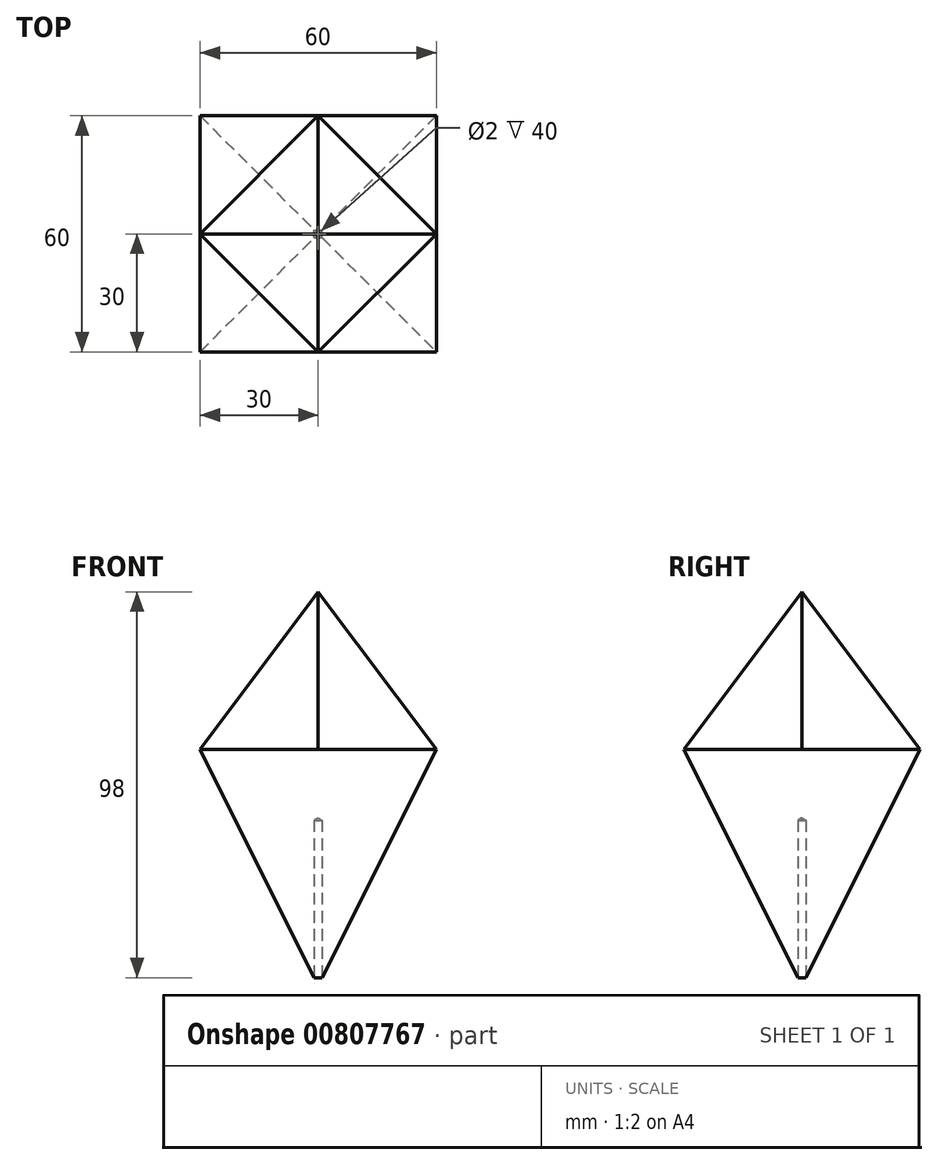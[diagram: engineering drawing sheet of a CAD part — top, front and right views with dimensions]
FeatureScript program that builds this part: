
annotation { "Feature Type Name" : "Feature", "Feature Type Description" : "" }
export const myFeature = defineFeature(function(context is Context, id is Id, definition is map)
    precondition{}
    {
        {
            var Q0;
            Q0=qCreatedBy(makeId("Top.planeOp"),FACE);
            cPlane(context, id + "F0", {"entities" : qUnion([Q0]), "cplaneType" : CPlaneType.OFFSET, "offset" : 60 * mm, "width" : 152.4 * mm, "height" : 152.4 * mm});
        }
        {
            var Q0;
            Q0=qCreatedBy(id+"F0.planeOp",FACE);
            var sketch = newSketch(context, id + "F1", { "sketchPlane" : qUnion([Q0])});
            skLineSegment(sketch, "E0.bottom", {"start": v(-30, 30) * mm, "end": v(30, 30) * mm});
            skLineSegment(sketch, "E0.top", {"start": v(-30, -30) * mm, "end": v(30, -30) * mm});
            skLineSegment(sketch, "E0.left", {"start": v(-30, 30) * mm, "end": v(-30, -30) * mm});
            skLineSegment(sketch, "E0.right", {"start": v(30, 30) * mm, "end": v(30, -30) * mm});
            skPoint(sketch, "E0.middle", {"position": v(0, 0) * mm});
            skLineSegment(sketch, "E1", {"start": v(-30, 0) * mm, "end": v(0, 30) * mm});
            skLineSegment(sketch, "E2", {"start": v(0, 30) * mm, "end": v(30, 0) * mm});
            skLineSegment(sketch, "E3", {"start": v(30, 0) * mm, "end": v(0, -30) * mm});
            skLineSegment(sketch, "E4", {"start": v(0, -30) * mm, "end": v(-30, 0) * mm});
            skSolve(sketch);
        }
        {
            var Q0;
            Q0=qCreatedBy(makeId("Top.planeOp"),FACE);
            cPlane(context, id + "F2", {"entities" : qUnion([Q0]), "cplaneType" : CPlaneType.OFFSET, "offset" : 100 * mm, "width" : 150 * mm, "height" : 150 * mm});
        }
        {
            var Q0;
            Q0=qCreatedBy(id+"F2.planeOp",FACE);
            var sketch = newSketch(context, id + "F3", { "sketchPlane" : qUnion([Q0])});
            skPoint(sketch, "E5.0", {"position": v(0, 0) * mm});
            skSolve(sketch);
        }
        {
            var Q0;
            Q0=qCreatedBy(makeId("Top.planeOp"),FACE);
            var sketch = newSketch(context, id + "F4", { "sketchPlane" : qUnion([Q0])});
            skPoint(sketch, "E6.0", {"position": v(0, 0) * mm});
            skLineSegment(sketch, "E7", {"start": v(0, 0) * mm, "end": v(-2.79, 22.45) * mm});
            skSolve(sketch);
        }
        {
            var Q0;
            Q0=qCreatedBy(makeId("Top.planeOp"),FACE);
            cPlane(context, id + "F5", {"entities" : qUnion([Q0]), "cplaneType" : CPlaneType.OFFSET, "offset" : 2 * mm, "width" : 150 * mm, "height" : 150 * mm});
        }
        {
            var Q0;
            Q0=qCreatedBy(id+"F5.planeOp",FACE);
            var sketch = newSketch(context, id + "F6", { "sketchPlane" : qUnion([Q0])});
            skLineSegment(sketch, "E8.bottom", {"start": v(-1, -1) * mm, "end": v(1, -1) * mm});
            skLineSegment(sketch, "E8.top", {"start": v(-1, 1) * mm, "end": v(1, 1) * mm});
            skLineSegment(sketch, "E8.left", {"start": v(-1, -1) * mm, "end": v(-1, 1) * mm});
            skLineSegment(sketch, "E8.right", {"start": v(1, -1) * mm, "end": v(1, 1) * mm});
            skPoint(sketch, "E8.middle", {"position": v(0, 0) * mm});
            skLineSegment(sketch, "E9", {"start": v(0, -1) * mm, "end": v(1, 0) * mm});
            skLineSegment(sketch, "E10", {"start": v(1, 0) * mm, "end": v(0, 1) * mm});
            skLineSegment(sketch, "E11", {"start": v(0, 1) * mm, "end": v(-1, 0) * mm});
            skLineSegment(sketch, "E12", {"start": v(0, -1) * mm, "end": v(-1, 0) * mm});
            skSolve(sketch);
        }
        {
            var Q0;
            {var subQ3=sQuery(id+"F1.wireOp",EDGE,"E4");Q0=makeQuery(id+"F1.imprint","IMPRINT",FACE,{"disambiguationData":[TD([[makeQuery(id+"F1.imprint","IMPRINT",EDGE,{"derivedFrom":subQ3}),1.0]])]});}
            var Q1;
            {var subQ3=sQuery(id+"F6.wireOp",EDGE,"E12");Q1=makeQuery(id+"F6.imprint","IMPRINT",FACE,{"disambiguationData":[TD([[makeQuery(id+"F6.imprint","IMPRINT",EDGE,{"derivedFrom":subQ3}),1.0]])]});}
            loft(context, id + "F7", {"sheetProfilesArray" : [{ "sheetProfileEntities" : qUnion([Q0]) }, { "sheetProfileEntities" : qUnion([Q1]) }]});
        }
        {
            var Q0;
            {var subQ3=sQuery(id+"F6.wireOp",EDGE,"E9");Q0=makeQuery(id+"F6.imprint","IMPRINT",FACE,{"disambiguationData":[TD([[makeQuery(id+"F6.imprint","IMPRINT",EDGE,{"derivedFrom":subQ3}),-1.0]])]});}
            var Q1;
            {var subQ3=sQuery(id+"F1.wireOp",EDGE,"E3");Q1=makeQuery(id+"F1.imprint","IMPRINT",FACE,{"disambiguationData":[TD([[makeQuery(id+"F1.imprint","IMPRINT",EDGE,{"derivedFrom":subQ3}),1.0]])]});}
            loft(context, id + "F8", {"sheetProfilesArray" : [{ "sheetProfileEntities" : qUnion([Q0]) }, { "sheetProfileEntities" : qUnion([Q1]) }]});
        }
        {
            var Q0;
            {var subQ3=sQuery(id+"F1.wireOp",EDGE,"E2");Q0=makeQuery(id+"F1.imprint","IMPRINT",FACE,{"disambiguationData":[TD([[makeQuery(id+"F1.imprint","IMPRINT",EDGE,{"derivedFrom":subQ3}),1.0]])]});}
            var Q1;
            {var subQ3=sQuery(id+"F6.wireOp",EDGE,"E10");Q1=makeQuery(id+"F6.imprint","IMPRINT",FACE,{"disambiguationData":[TD([[makeQuery(id+"F6.imprint","IMPRINT",EDGE,{"derivedFrom":subQ3}),-1.0]])]});}
            loft(context, id + "F9", {"sheetProfilesArray" : [{ "sheetProfileEntities" : qUnion([Q0]) }, { "sheetProfileEntities" : qUnion([Q1]) }]});
        }
        {
            var Q0;
            {var subQ3=sQuery(id+"F1.wireOp",EDGE,"E1");Q0=makeQuery(id+"F1.imprint","IMPRINT",FACE,{"disambiguationData":[TD([[makeQuery(id+"F1.imprint","IMPRINT",EDGE,{"derivedFrom":subQ3}),1.0]])]});}
            var Q1;
            {var subQ3=sQuery(id+"F6.wireOp",EDGE,"E11");Q1=makeQuery(id+"F6.imprint","IMPRINT",FACE,{"disambiguationData":[TD([[makeQuery(id+"F6.imprint","IMPRINT",EDGE,{"derivedFrom":subQ3}),-1.0]])]});}
            loft(context, id + "F10", {"sheetProfilesArray" : [{ "sheetProfileEntities" : qUnion([Q0]) }, { "sheetProfileEntities" : qUnion([Q1]) }]});
        }
        {
            var Q0;
            Q0=makeQuery(id+"F1.imprint","IMPRINT",FACE,{"disambiguationData":[TD([[makeQuery(id+"F1.imprint","IMPRINT",EDGE,{"derivedFrom":sQuery(id+"F1.wireOp",EDGE,"E1")}),-1.0]])]});
            var Q1;
            Q1=makeQuery(id+"F6.imprint","IMPRINT",FACE,{"disambiguationData":[TD([[makeQuery(id+"F6.imprint","IMPRINT",EDGE,{"derivedFrom":sQuery(id+"F6.wireOp",EDGE,"E9")}),1.0]])]});
            loft(context, id + "F11", {"sheetProfilesArray" : [{ "sheetProfileEntities" : qUnion([Q0]) }, { "sheetProfileEntities" : qUnion([Q1]) }]});
        }
        {
            var Q1;
            Q1=makeQuery(id+"F1.imprint","IMPRINT",FACE,{"disambiguationData":[TD([[makeQuery(id+"F1.imprint","IMPRINT",EDGE,{"derivedFrom":sQuery(id+"F1.wireOp",EDGE,"E1")}),-1.0]])]});
            var Q2;
            Q2=sQuery(id+"F3.wireOp",VERTEX,"E5.0");
            loft(context, id + "F12", {"operationType" : NewBodyOperationType.ADD, "sheetProfilesArray" : [{ "sheetProfileEntities" : qUnion([Q1]) }, { "sheetProfileEntities" : qUnion([Q2]) }]});
        }
        {
            var Q0;
            Q0=sQuery(id+"F6.wireOp",VERTEX,"E8.middle");
            var Q1;
            Q1=makeQuery(id+"F11.opLoft","SWEPT_BODY",BODY,{"disambiguationData":[OSD([makeQuery(id+"F1.imprint","IMPRINT",FACE,{"disambiguationData":[TD([[makeQuery(id+"F1.imprint","IMPRINT",EDGE,{"derivedFrom":sQuery(id+"F1.wireOp",EDGE,"E1")}),-1.0]])]}),makeQuery(id+"F6.imprint","IMPRINT",FACE,{"disambiguationData":[TD([[makeQuery(id+"F6.imprint","IMPRINT",EDGE,{"derivedFrom":sQuery(id+"F6.wireOp",EDGE,"E9")}),1.0]])]})])]});
            var Q2;
            {var subQ3=sQuery(id+"F6.wireOp",EDGE,"E12");var subQ7=sQuery(id+"F1.wireOp",EDGE,"E4");Q2=makeQuery(id+"F7.opLoft","SWEPT_BODY",BODY,{"disambiguationData":[OSD([makeQuery(id+"F1.imprint","IMPRINT",FACE,{"disambiguationData":[TD([[makeQuery(id+"F1.imprint","IMPRINT",EDGE,{"derivedFrom":subQ7}),1.0]])]}),makeQuery(id+"F6.imprint","IMPRINT",FACE,{"disambiguationData":[TD([[makeQuery(id+"F6.imprint","IMPRINT",EDGE,{"derivedFrom":subQ3}),1.0]])]})])]});}
            var Q3;
            {var subQ3=sQuery(id+"F6.wireOp",EDGE,"E9");var subQ7=sQuery(id+"F1.wireOp",EDGE,"E3");Q3=makeQuery(id+"F8.opLoft","SWEPT_BODY",BODY,{"disambiguationData":[OSD([makeQuery(id+"F1.imprint","IMPRINT",FACE,{"disambiguationData":[TD([[makeQuery(id+"F1.imprint","IMPRINT",EDGE,{"derivedFrom":subQ7}),1.0]])]}),makeQuery(id+"F6.imprint","IMPRINT",FACE,{"disambiguationData":[TD([[makeQuery(id+"F6.imprint","IMPRINT",EDGE,{"derivedFrom":subQ3}),-1.0]])]})])]});}
            var Q4;
            {var subQ3=sQuery(id+"F6.wireOp",EDGE,"E10");var subQ7=sQuery(id+"F1.wireOp",EDGE,"E2");Q4=makeQuery(id+"F9.opLoft","SWEPT_BODY",BODY,{"disambiguationData":[OSD([makeQuery(id+"F1.imprint","IMPRINT",FACE,{"disambiguationData":[TD([[makeQuery(id+"F1.imprint","IMPRINT",EDGE,{"derivedFrom":subQ7}),1.0]])]}),makeQuery(id+"F6.imprint","IMPRINT",FACE,{"disambiguationData":[TD([[makeQuery(id+"F6.imprint","IMPRINT",EDGE,{"derivedFrom":subQ3}),-1.0]])]})])]});}
            var Q5;
            {var subQ3=sQuery(id+"F6.wireOp",EDGE,"E11");var subQ7=sQuery(id+"F1.wireOp",EDGE,"E1");Q5=makeQuery(id+"F10.opLoft","SWEPT_BODY",BODY,{"disambiguationData":[OSD([makeQuery(id+"F1.imprint","IMPRINT",FACE,{"disambiguationData":[TD([[makeQuery(id+"F1.imprint","IMPRINT",EDGE,{"derivedFrom":subQ7}),1.0]])]}),makeQuery(id+"F6.imprint","IMPRINT",FACE,{"disambiguationData":[TD([[makeQuery(id+"F6.imprint","IMPRINT",EDGE,{"derivedFrom":subQ3}),-1.0]])]})])]});}
            hole(context, id + "F13", {"style" : HoleStyle.SIMPLE, "endStyle" : HoleEndStyle.BLIND, "oppositeDirection" : true, "holeDiameter" : 2 * mm, "majorDiameter" : 5 * mm, "holeDepth" : 40 * mm, "isTappedThrough" : true, "tappedDepth" : 12 * mm, "tapClearance" : 3, "locations" : qUnion([Q0]), "scope" : qUnion([Q1, Q2, Q3, Q4, Q5])});
        }
    });
